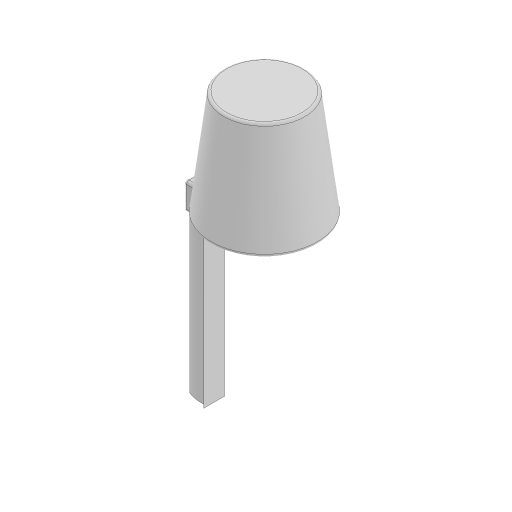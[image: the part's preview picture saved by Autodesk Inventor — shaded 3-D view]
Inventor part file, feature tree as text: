
AUTODESK INVENTOR PART (.ipt)
format: ipt  version: 2024 (Build 280153000, 153)  size: 216,064 bytes
history: native  units: mm
features: sketch x4, plane x3, extrude x2, loft x1, fillet x1
ambient origin geometry x8: Origin, YZ Plane, XZ Plane, XY Plane, X Axis, Y Axis, Z Axis, Center Point
bodies: Solid1 (feature_tree)
feature tree (11):
  extrude  "Extrusion1"  Depth=3.853584mm
  plane  "Work Plane1"
  extrude  "Extrusion2"  Depth=3.681754mm
  plane  "Work Plane3"
  sketch  "Sketch5"  dims[d10=30.0mm d11=0.0mm d12=0.0mm d41=15.0mm]
  plane  "Work Plane4"
  loft  "Loft2"
  fillet  "Fillet7"  Radius=15.0mm
  sketch  "Sketch1"  dims[d6=1.708645mm d7=3.853584mm]
  sketch  "Sketch4"  dims[d8=3.673792mm d9=3.681754mm]
  sketch  "Sketch6"  dims[d42=5.0mm d43=0.0mm d44=0.0mm d45=20.0mm d48=20.0mm d49=15.0mm d50=0.0mm d51=90.0deg d52=0.0mm d53=90.0deg d54=0.5mm]
